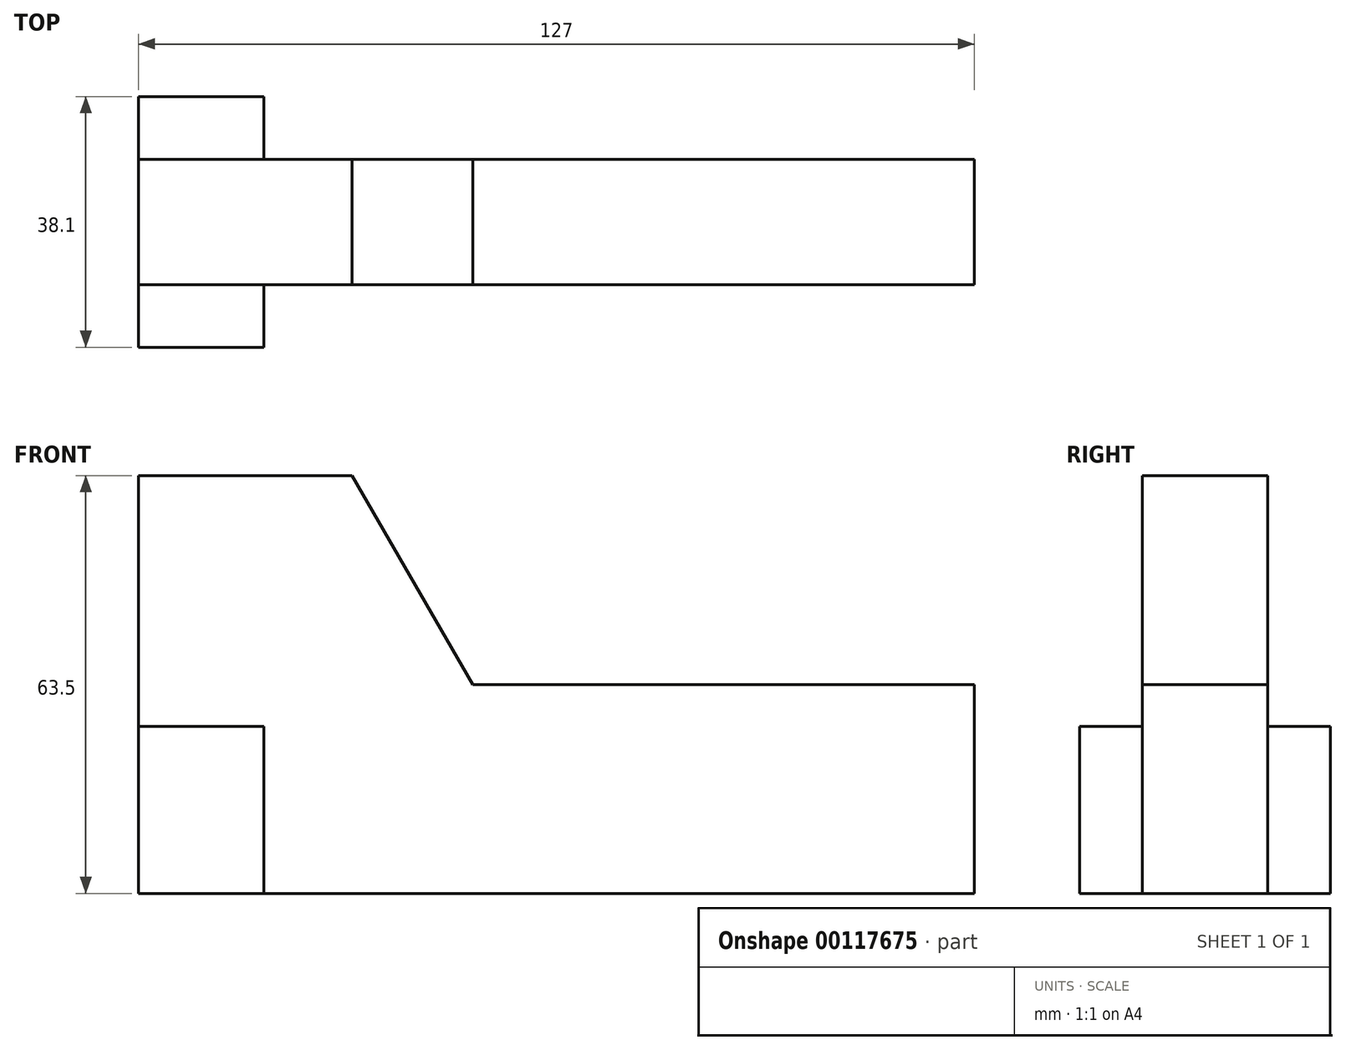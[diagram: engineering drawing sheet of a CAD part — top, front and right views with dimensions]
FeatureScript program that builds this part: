
annotation { "Feature Type Name" : "Feature", "Feature Type Description" : "" }
export const myFeature = defineFeature(function(context is Context, id is Id, definition is map)
    precondition{}
    {
        {
            var Q0;
            Q0=qCreatedBy(makeId("Front.planeOp"),FACE);
            var sketch = newSketch(context, id + "F0", { "sketchPlane" : qUnion([Q0])});
            skLineSegment(sketch, "E0.bottom", {"start": v(-63.5, 31.75) * mm, "end": v(-31.03, 31.75) * mm});
            skLineSegment(sketch, "E0.top", {"start": v(-63.5, -31.75) * mm, "end": v(63.5, -31.75) * mm});
            skLineSegment(sketch, "E0.left", {"start": v(-63.5, 31.75) * mm, "end": v(-63.5, -31.75) * mm});
            skLineSegment(sketch, "E0.right", {"start": v(63.5, 0) * mm, "end": v(63.5, -31.75) * mm});
            skPoint(sketch, "E0.middle", {"position": v(0, 0) * mm});
            skLineSegment(sketch, "E1", {"start": v(-63.5, -31.75) * mm, "end": v(-63.5, 0) * mm});
            skLineSegment(sketch, "E2", {"start": v(-63.5, 0) * mm, "end": v(63.5, 0) * mm});
            skLineSegment(sketch, "E3", {"start": v(63.5, 0) * mm, "end": v(-12.7, 0) * mm});
            skLineSegment(sketch, "E4", {"start": v(-12.7, 0) * mm, "end": v(-31.03, 31.75) * mm});
            skPoint(sketch, "E5.orphan", {"position": v(63.5, 31.75) * mm});
            skSolve(sketch);
        }
        {
            var Q0;
            Q0=makeQuery(id+"F0.imprint","IMPRINT",FACE,{"disambiguationData":[TD([[makeQuery(id+"F0.imprint","IMPRINT",EDGE,{"derivedFrom":sQuery(id+"F0.wireOp",EDGE,"E0.top")}),1.0]])]});
            var Q1;
            Q1=makeQuery(id+"F0.imprint","IMPRINT",FACE,{"disambiguationData":[TD([[makeQuery(id+"F0.imprint","IMPRINT",EDGE,{"derivedFrom":sQuery(id+"F0.wireOp",EDGE,"E0.bottom")}),-1.0]])]});
            extrude(context, id + "F1", {"entities" : qUnion([Q0, Q1]), "depth" : 19.05 * mm});
        }
        {
            var Q0;
            Q0=makeQuery(id+"F1.opExtrude","CAP_FACE",FACE,{"disambiguationData":[OSD([sQuery(id+"F0.wireOp",EDGE,"E0.bottom"),sQuery(id+"F0.wireOp",EDGE,"E0.top"),sQuery(id+"F0.wireOp",EDGE,"E0.left"),sQuery(id+"F0.wireOp",EDGE,"E0.right"),sQuery(id+"F0.wireOp",EDGE,"E1"),sQuery(id+"F0.wireOp",EDGE,"E3"),sQuery(id+"F0.wireOp",EDGE,"E4")])],"isStart":false});
            var sketch = newSketch(context, id + "F2", { "sketchPlane" : qUnion([Q0])});
            skLineSegment(sketch, "E6.bottom", {"start": v(-63.5, -31.75) * mm, "end": v(-44.45, -31.75) * mm});
            skLineSegment(sketch, "E6.top", {"start": v(-63.5, -6.35) * mm, "end": v(-44.45, -6.35) * mm});
            skLineSegment(sketch, "E6.left", {"start": v(-63.5, -31.75) * mm, "end": v(-63.5, -6.35) * mm});
            skLineSegment(sketch, "E6.right", {"start": v(-44.45, -31.75) * mm, "end": v(-44.45, -6.35) * mm});
            skSolve(sketch);
        }
        {
            var Q0;
            Q0=makeQuery(id+"F2.imprint","IMPRINT",FACE,{"disambiguationData":[TD([[makeQuery(id+"F2.imprint","IMPRINT",EDGE,{"derivedFrom":sQuery(id+"F2.wireOp",EDGE,"E6.bottom")}),1.0]])]});
            extrude(context, id + "F3", {"entities" : qUnion([Q0]), "operationType" : NewBodyOperationType.ADD, "depth" : 9.52 * mm});
        }
        {
            var Q0;
            Q0=makeQuery(id+"F1.opExtrude","CAP_FACE",FACE,{"disambiguationData":[OSD([sQuery(id+"F0.wireOp",EDGE,"E0.bottom"),sQuery(id+"F0.wireOp",EDGE,"E0.top"),sQuery(id+"F0.wireOp",EDGE,"E0.left"),sQuery(id+"F0.wireOp",EDGE,"E0.right"),sQuery(id+"F0.wireOp",EDGE,"E1"),sQuery(id+"F0.wireOp",EDGE,"E3"),sQuery(id+"F0.wireOp",EDGE,"E4")])],"isStart":true});
            var sketch = newSketch(context, id + "F4", { "sketchPlane" : qUnion([Q0])});
            skLineSegment(sketch, "E7.bottom", {"start": v(63.5, -31.75) * mm, "end": v(44.45, -31.75) * mm});
            skLineSegment(sketch, "E7.top", {"start": v(63.5, -6.35) * mm, "end": v(44.45, -6.35) * mm});
            skLineSegment(sketch, "E7.left", {"start": v(63.5, -31.75) * mm, "end": v(63.5, -6.35) * mm});
            skLineSegment(sketch, "E7.right", {"start": v(44.45, -31.75) * mm, "end": v(44.45, -6.35) * mm});
            skSolve(sketch);
        }
        {
            var Q0;
            Q0=makeQuery(id+"F4.imprint","IMPRINT",FACE,{"disambiguationData":[TD([[makeQuery(id+"F4.imprint","IMPRINT",EDGE,{"derivedFrom":sQuery(id+"F4.wireOp",EDGE,"E7.bottom")}),-1.0]])]});
            extrude(context, id + "F5", {"entities" : qUnion([Q0]), "operationType" : NewBodyOperationType.ADD, "depth" : 9.52 * mm});
        }
    });
